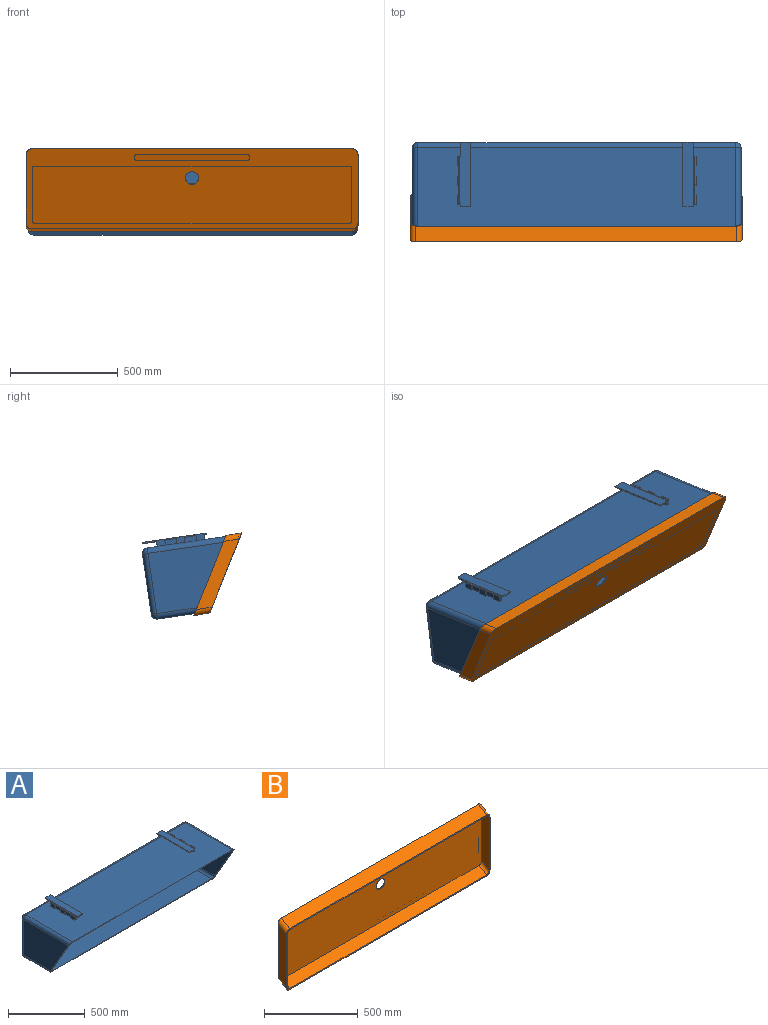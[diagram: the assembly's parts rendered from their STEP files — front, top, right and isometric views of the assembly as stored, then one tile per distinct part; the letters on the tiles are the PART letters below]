
ASSEMBLY  parts=2 mates=1
PART A: 95 faces, bbox 1524.8x459.1x362 mm
  f0: plane 1524.76x333.4mm, normal (0,-0.87,-0.5), area 26805.2mm2, adj f11,f12,f13,f15,f66,f68,f71,f74
  f1: plane 222.25x23.5mm, normal (1,0,0), area 5221.8mm2, adj f11,f44,f45,f50
  f2: plane 42.55x6.35mm, normal (0,1,0), area 270.2mm2, adj f4,f41,f42,f47
  f3: plane 222.25x17.15mm, normal (-1,0,0), area 3810.5mm2, adj f11,f44,f45,f48
  f4: plane 301.63x48.9mm, normal (0,0,1), area 14636.1mm2, adj f2,f5,f42,f43,f44,f45,f46,f47
  f5: plane 42.55x6.35mm, normal (0,-1,0), area 270.2mm2, adj f4,f41,f42,f49
  f6: plane 42.55x6.35mm, normal (0,-1,0), area 270.2mm2, adj f7,f31,f32,f38
  f7: plane 301.63x48.9mm, normal (0,0,1), area 14636.1mm2, adj f6,f9,f32,f33,f34,f35,f36,f38
  f8: plane 222.25x17.15mm, normal (1,0,0), area 3810.5mm2, adj f11,f34,f35,f37
  f9: plane 42.55x6.35mm, normal (0,1,0), area 270.2mm2, adj f7,f31,f32,f39
  f10: plane 222.25x23.5mm, normal (-1,0,0), area 5221.8mm2, adj f11,f34,f35,f40
  f11: plane 1473.96x433.71mm, normal (0,0,1), area 634990.5mm2, adj f0,f1,f3,f8,f10,f16,f17,f18
  f12: plane 418.99x282.6mm, normal (-1,0,0), area 95277.8mm2, adj f0,f66,f67,f68
  f13: plane 418.99x282.6mm, normal (1,0,0), area 95277.8mm2, adj f0,f71,f74,f77
  f14: plane 1473.96x282.6mm, normal (0,1,0), area 416542.3mm2, adj f67,f72,f73,f77
  f15: plane 1473.96x240.59mm, normal (0,0,-1), area 354617.7mm2, adj f0,f68,f73,f74
  f16: plane 28.58x6.35mm, normal (0,1,0), area 181.5mm2, adj f11,f17,f19,f20
  f17: plane 38.1x28.58mm, normal (-1,0,0), area 1088.7mm2, adj f11,f16,f18,f20
  f18: plane 28.58x6.35mm, normal (0,-1,0), area 181.5mm2, adj f11,f17,f19,f20
  f19: plane 38.1x28.58mm, normal (1,0,0), area 1088.7mm2, adj f11,f16,f18,f20
  f20: plane 38.1x6.35mm, normal (0,0,1), area 241.9mm2, adj f16,f17,f18,f19
  f21: plane 28.58x6.35mm, normal (0,1,0), area 181.5mm2, adj f11,f22,f24,f25
  f22: plane 38.1x28.58mm, normal (-1,0,0), area 1088.7mm2, adj f11,f21,f23,f25
  f23: plane 28.58x6.35mm, normal (0,-1,0), area 181.5mm2, adj f11,f22,f24,f25
  f24: plane 38.1x28.58mm, normal (1,0,0), area 1088.7mm2, adj f11,f21,f23,f25
  f25: plane 38.1x6.35mm, normal (0,0,1), area 241.9mm2, adj f21,f22,f23,f24
  f26: plane 28.58x6.35mm, normal (0,1,0), area 181.5mm2, adj f11,f27,f29,f30
  f27: plane 38.1x28.58mm, normal (-1,0,0), area 1088.7mm2, adj f11,f26,f28,f30
  f28: plane 28.58x6.35mm, normal (0,-1,0), area 181.5mm2, adj f11,f27,f29,f30
  f29: plane 38.1x28.58mm, normal (1,0,0), area 1088.7mm2, adj f11,f26,f28,f30
  f30: plane 38.1x6.35mm, normal (0,0,1), area 241.9mm2, adj f26,f27,f28,f29
  f31: plane 301.63x47.63mm, normal (0,0,-1), area 13224.8mm2, adj f6,f9,f32,f33,f34,f35,f36,f37
  f32: plane 301.63x6.35mm, normal (1,0,0), area 1915.3mm2, adj f6,f7,f9,f31
  f33: plane 61.6x6.35mm, normal (-1,0,0), area 391.1mm2, adj f7,f31,f34,f39
  f34: plane 28.58x11.43mm, normal (0,1,0), area 181.5mm2, adj f7,f8,f10,f11,f31,f33,f37,f40
  f35: plane 28.58x11.43mm, normal (0,-1,0), area 181.5mm2, adj f7,f8,f10,f11,f31,f36,f37,f40
  f36: plane 7.62x6.35mm, normal (-1,0,0), area 48.4mm2, adj f7,f31,f35,f38
  f37: cylinder r=5.08mm len=222.25mm, axis (0,1,0), area 1773.5mm2, adj f8,f31,f34,f35
  f38: cylinder r=5.08mm len=6.35mm, axis (0,0,1), area 50.7mm2, adj f6,f7,f31,f36
  f39: cylinder r=5.08mm len=6.35mm, axis (0,0,1), area 50.7mm2, adj f7,f9,f31,f33
  f40: cylinder r=5.08mm len=222.25mm, axis (0,1,0), area 1773.5mm2, adj f7,f10,f34,f35
  f41: plane 301.63x47.63mm, normal (0,0,-1), area 13224.8mm2, adj f2,f5,f42,f43,f44,f45,f46,f47
  f42: plane 301.63x6.35mm, normal (-1,0,0), area 1915.3mm2, adj f2,f4,f5,f41
  f43: plane 7.62x6.35mm, normal (1,0,0), area 48.4mm2, adj f4,f41,f44,f49
  f44: plane 28.58x11.43mm, normal (0,-1,0), area 181.5mm2, adj f1,f3,f4,f11,f41,f43,f48,f50
  f45: plane 28.58x11.43mm, normal (0,1,0), area 181.5mm2, adj f1,f3,f4,f11,f41,f46,f48,f50
  f46: plane 61.6x6.35mm, normal (1,0,0), area 391.1mm2, adj f4,f41,f45,f47
  f47: cylinder r=5.08mm len=6.35mm, axis (0,0,1), area 50.7mm2, adj f2,f4,f41,f46
  f48: cylinder r=5.08mm len=222.25mm, axis (0,1,0), area 1773.5mm2, adj f3,f41,f44,f45
  f49: cylinder r=5.08mm len=6.35mm, axis (0,0,1), area 50.7mm2, adj f4,f5,f41,f43
  f50: cylinder r=5.08mm len=222.25mm, axis (0,-1,0), area 1773.5mm2, adj f1,f4,f44,f45
  f51: plane 28.58x6.35mm, normal (0,1,0), area 181.5mm2, adj f11,f52,f54,f55
  f52: plane 38.1x28.58mm, normal (-1,0,0), area 1088.7mm2, adj f11,f51,f53,f55
  f53: plane 28.58x6.35mm, normal (0,-1,0), area 181.5mm2, adj f11,f52,f54,f55
  f54: plane 38.1x28.58mm, normal (1,0,0), area 1088.7mm2, adj f11,f51,f53,f55
  f55: plane 38.1x6.35mm, normal (0,0,1), area 241.9mm2, adj f51,f52,f53,f54
  f56: plane 38.1x28.58mm, normal (1,0,0), area 1088.7mm2, adj f11,f57,f59,f60
  f57: plane 28.58x6.35mm, normal (0,1,0), area 181.5mm2, adj f11,f56,f58,f60
  f58: plane 38.1x28.58mm, normal (-1,0,0), area 1088.7mm2, adj f11,f57,f59,f60
  f59: plane 28.58x6.35mm, normal (0,-1,0), area 181.5mm2, adj f11,f56,f58,f60
  f60: plane 38.1x6.35mm, normal (0,0,1), area 241.9mm2, adj f56,f57,f58,f59
  f61: plane 38.1x28.58mm, normal (1,0,0), area 1088.7mm2, adj f11,f62,f64,f65
  f62: plane 28.58x6.35mm, normal (0,1,0), area 181.5mm2, adj f11,f61,f63,f65
  f63: plane 38.1x28.58mm, normal (-1,0,0), area 1088.7mm2, adj f11,f62,f64,f65
  f64: plane 28.58x6.35mm, normal (0,-1,0), area 181.5mm2, adj f11,f61,f63,f65
  f65: plane 38.1x6.35mm, normal (0,0,1), area 241.9mm2, adj f61,f62,f63,f64
  f66: cylinder r=25.4mm len=433.71mm, axis (0,1,0), area 17090.8mm2, adj f0,f11,f12,f69
  f67: cylinder r=25.4mm len=282.6mm, axis (0,0,-1), area 11275.3mm2, adj f12,f14,f69,f70
  f68: cylinder r=25.4mm len=255.3mm, axis (0,-1,0), area 9812.3mm2, adj f0,f12,f15,f70
  f69: sphere r=25.4mm, area 1013.4mm2, adj f66,f67,f72
  f70: sphere r=25.4mm, area 1013.4mm2, adj f67,f68,f73
  f71: cylinder r=25.4mm len=433.71mm, axis (0,-1,0), area 17090.8mm2, adj f0,f11,f13,f75
  f72: cylinder r=25.4mm len=1473.96mm, axis (1,0,0), area 58808.5mm2, adj f11,f14,f69,f75
  f73: cylinder r=25.4mm len=1473.96mm, axis (-1,0,0), area 58808.5mm2, adj f14,f15,f70,f76
  f74: cylinder r=25.4mm len=255.3mm, axis (0,1,0), area 9812.3mm2, adj f0,f13,f15,f76
  f75: sphere r=25.4mm, area 1013.4mm2, adj f71,f72,f77
  f76: sphere r=25.4mm, area 1013.4mm2, adj f73,f74,f77
  f77: cylinder r=25.4mm len=282.6mm, axis (0,0,1), area 11275.3mm2, adj f13,f14,f75,f76
  f78: plane 1473.96x430.03mm, normal (0,0,-1), area 633843.3mm2, adj f0,f83,f88,f89
  f79: plane 418.99x282.6mm, normal (1,0,0), area 95277.8mm2, adj f0,f83,f84,f85
  f80: plane 418.99x282.6mm, normal (-1,0,0), area 95277.8mm2, adj f0,f88,f91,f94
  f81: plane 1473.96x282.6mm, normal (0,-1,0), area 416542.3mm2, adj f84,f89,f90,f94
  f82: plane 1473.96x244.27mm, normal (0,0,1), area 360039.2mm2, adj f0,f85,f90,f91
  f83: cylinder r=19.05mm len=430.03mm, axis (0,1,0), area 12748mm2, adj f0,f78,f79,f86
  f84: cylinder r=19.05mm len=282.6mm, axis (0,0,-1), area 8456.4mm2, adj f79,f81,f86,f87
  f85: cylinder r=19.05mm len=255.3mm, axis (0,-1,0), area 7429.3mm2, adj f0,f79,f82,f87
  f86: sphere r=19.05mm, area 570mm2, adj f83,f84,f89
  f87: sphere r=19.05mm, area 570mm2, adj f84,f85,f90
  f88: cylinder r=19.05mm len=430.03mm, axis (0,-1,0), area 12748mm2, adj f0,f78,f80,f92
  f89: cylinder r=19.05mm len=1473.96mm, axis (1,0,0), area 44106.4mm2, adj f78,f81,f86,f92
  f90: cylinder r=19.05mm len=1473.96mm, axis (-1,0,0), area 44106.4mm2, adj f81,f82,f87,f93
  f91: cylinder r=19.05mm len=255.3mm, axis (0,1,0), area 7429.3mm2, adj f0,f80,f82,f93
  f92: sphere r=19.05mm, area 570mm2, adj f88,f89,f94
  f93: sphere r=19.05mm, area 570mm2, adj f90,f91,f94
  f94: cylinder r=19.05mm len=282.6mm, axis (0,0,1), area 8456.4mm2, adj f80,f81,f92,f93
PART B: 34 faces, bbox 1539.9x89.6x438.2 mm
  f0: plane 1539.88x400.05mm, normal (0,1,0), area 176673.5mm2, adj f1,f2,f4,f5,f6,f7,f8,f9
  f1: plane 1489.08x63.5mm, normal (0,0.51,-0.86), area 110270.6mm2, adj f0,f3,f7,f9
  f2: plane 1489.08x63.5mm, normal (0,-0.51,0.86), area 110270.6mm2, adj f0,f3,f6,f8
  f3: plane 1539.88x400.05mm, normal (0,-1,0), area 27416.5mm2, adj f1,f2,f4,f5,f6,f7,f8,f9
  f4: plane 378.91x63.5mm, normal (1,0,0), area 21641.3mm2, adj f0,f3,f8,f9
  f5: plane 378.91x63.5mm, normal (-1,0,0), area 21641.3mm2, adj f0,f3,f6,f7
  f6: cylinder r=25.4mm len=89.64mm, axis (0,-0.86,-0.51), area 2954.6mm2, adj f0,f2,f3,f5
  f7: cylinder r=25.4mm len=89.64mm, axis (0,0.86,0.51), area 2954.6mm2, adj f0,f1,f3,f5
  f8: cylinder r=25.4mm len=89.64mm, axis (0,0.86,0.51), area 2954.6mm2, adj f0,f2,f3,f4
  f9: cylinder r=25.4mm len=89.64mm, axis (0,-0.86,-0.51), area 2954.6mm2, adj f0,f1,f3,f4
  f10: plane 1489.08x57.15mm, normal (0,-0.51,0.86), area 99243.5mm2, adj f3,f11,f16,f18
  f11: plane 1527.18x385.24mm, normal (0,-1,0), area 584797.7mm2, adj f10,f12,f13,f14,f15,f16,f17,f18
  f12: plane 1489.08x57.15mm, normal (0,0.51,-0.86), area 99243.5mm2, adj f3,f11,f15,f17
  f13: plane 375.1x57.15mm, normal (-1,0,0), area 19477.2mm2, adj f3,f11,f17,f18
  f14: plane 375.1x57.15mm, normal (1,0,0), area 19477.2mm2, adj f3,f11,f15,f16
  f15: cylinder r=19.05mm len=76.75mm, axis (0,-0.86,-0.51), area 1994.3mm2, adj f3,f11,f12,f14
  f16: cylinder r=19.05mm len=76.75mm, axis (0,0.86,0.51), area 1994.3mm2, adj f3,f10,f11,f14
  f17: cylinder r=19.05mm len=76.75mm, axis (0,0.86,0.51), area 1994.3mm2, adj f3,f11,f12,f13
  f18: cylinder r=19.05mm len=76.75mm, axis (0,-0.86,-0.51), area 1994.3mm2, adj f3,f10,f11,f13
  f19: plane 508x0.79mm, normal (0,0,-1), area 403.2mm2, adj f0,f21,f22,f23
  f20: plane 508x0.79mm, normal (0,0,1), area 403.2mm2, adj f0,f21,f22,f23
  f21: plane 536.58x28.58mm, normal (0,1,0), area 15157.4mm2, adj f19,f20,f22,f23
  f22: cylinder r=14.29mm len=28.58mm, axis (0,1,0), area 35.6mm2, adj f0,f19,f20,f21
  f23: cylinder r=14.29mm len=28.58mm, axis (0,1,0), area 35.6mm2, adj f0,f19,f20,f21
  f24: plane 1457.33x1.59mm, normal (0,0,-1), area 2313.5mm2, adj f0,f28,f29,f32
  f25: plane 260.35x1.59mm, normal (-1,0,0), area 413.3mm2, adj f0,f28,f29,f30
  f26: plane 1457.33x1.59mm, normal (0,0,1), area 2313.5mm2, adj f0,f28,f30,f31
  f27: plane 260.35x1.59mm, normal (1,0,0), area 413.3mm2, adj f0,f28,f31,f32
  f28: plane 1482.73x285.75mm, normal (0,1,0), area 420383.3mm2, adj f24,f25,f26,f27,f29,f30,f31,f32
  f29: cylinder r=12.7mm len=12.7mm, axis (0,1,0), area 31.7mm2, adj f0,f24,f25,f28
  f30: cylinder r=12.7mm len=12.7mm, axis (0,-1,0), area 31.7mm2, adj f0,f25,f26,f28
  f31: cylinder r=12.7mm len=12.7mm, axis (0,1,0), area 31.7mm2, adj f0,f26,f27,f28
  f32: cylinder r=12.7mm len=12.7mm, axis (0,-1,0), area 31.7mm2, adj f0,f24,f27,f28
  f33: cylinder r=31.75mm len=63.5mm, axis (0,1,0), area 950.1mm2, adj f11,f28
PLACE A rot(axis=(-1,0,0),8.3deg) t=(-1053.06,7.34,-335.69)mm
PLACE B rot(axis=(0,0.19,-0.98),180deg) t=(475.9,208.33,-405.31)mm
MATE planar B.f11 <-> A.f0  axis (0,0.93,0.37) through (-294.04,127.32,-185.69)mm
